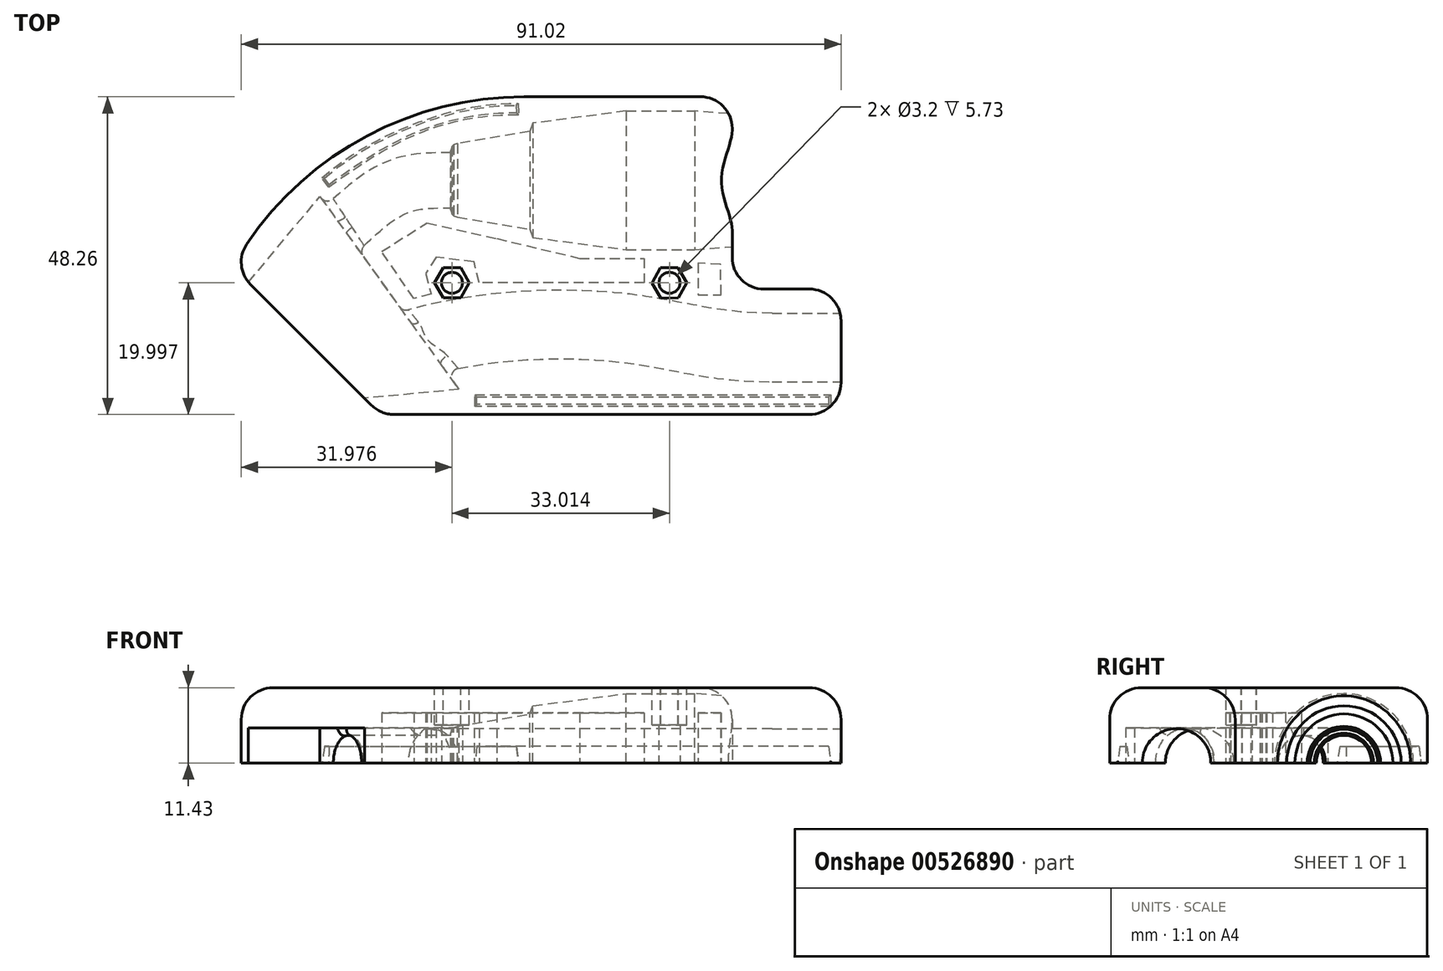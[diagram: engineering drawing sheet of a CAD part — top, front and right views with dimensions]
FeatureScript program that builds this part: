
annotation { "Feature Type Name" : "Feature", "Feature Type Description" : "" }
export const myFeature = defineFeature(function(context is Context, id is Id, definition is map)
    precondition{}
    {
        {
            var Q0;
            Q0=qCreatedBy(makeId("Top.planeOp"),FACE);
            var sketch = newSketch(context, id + "F0", { "sketchPlane" : qUnion([Q0])});
            skLineSegment(sketch, "E0", {"start": v(-28.61, 2.44) * mm, "end": v(45.8, 2.44) * mm});
            skLineSegment(sketch, "E1", {"start": v(45.8, 2.44) * mm, "end": v(45.8, -5.69) * mm});
            skLineSegment(sketch, "E2", {"start": v(45.8, -5.69) * mm, "end": v(33.96, -5.69) * mm});
            skLineSegment(sketch, "E3", {"start": v(33.96, -5.69) * mm, "end": v(31.07, -7.5) * mm});
            skLineSegment(sketch, "E4", {"start": v(31.07, -7.5) * mm, "end": v(15.98, -7.5) * mm});
            skLineSegment(sketch, "E5", {"start": v(15.98, -7.5) * mm, "end": v(8.33, -8.1) * mm});
            skLineSegment(sketch, "E6", {"start": v(8.33, -8.1) * mm, "end": v(-2.02, -8.1) * mm});
            skLineSegment(sketch, "E7", {"start": v(-2.02, -8.1) * mm, "end": v(-16.21, -6.24) * mm});
            skLineSegment(sketch, "E8", {"start": v(-16.21, -6.24) * mm, "end": v(-16.67, -5) * mm});
            skLineSegment(sketch, "E9", {"start": v(-16.67, -5) * mm, "end": v(-27.65, -3.12) * mm});
            skLineSegment(sketch, "E10", {"start": v(-27.65, -3.12) * mm, "end": v(-28.19, -2.96) * mm});
            skLineSegment(sketch, "E11", {"start": v(-28.19, -2.96) * mm, "end": v(-28.49, -2.68) * mm});
            skLineSegment(sketch, "E12", {"start": v(-28.49, -2.68) * mm, "end": v(-28.63, -2.06) * mm});
            skLineSegment(sketch, "E13", {"start": v(-28.63, -2.06) * mm, "end": v(-28.61, 2.44) * mm});
            skLineSegment(sketch, "E14.bottom", {"start": v(20.09, -22.96) * mm, "end": v(33.96, -22.96) * mm});
            skLineSegment(sketch, "E14.top", {"start": v(20.09, -28.16) * mm, "end": v(33.96, -28.16) * mm});
            skLineSegment(sketch, "E14.left", {"start": v(20.09, -22.96) * mm, "end": v(20.09, -28.16) * mm});
            skLineSegment(sketch, "E14.right", {"start": v(33.96, -22.96) * mm, "end": v(33.96, -28.16) * mm});
            skLineSegment(sketch, "E15", {"start": v(33.96, -25.56) * mm, "end": v(42.75, -25.56) * mm});
            skLineSegment(sketch, "E16", {"start": v(42.75, -25.56) * mm, "end": v(42.75, -22.97) * mm});
            skLineSegment(sketch, "E17", {"start": v(42.75, -22.97) * mm, "end": v(33.96, -22.96) * mm});
            skLineSegment(sketch, "E18.MirrorCS", {"start": v(45.8, 2.44) * mm, "end": v(45.8, 10.57) * mm});
            skLineSegment(sketch, "E19.MirrorCS", {"start": v(45.8, 10.57) * mm, "end": v(33.96, 10.57) * mm});
            skLineSegment(sketch, "E20.MirrorCS", {"start": v(33.96, 10.57) * mm, "end": v(31.07, 12.39) * mm});
            skLineSegment(sketch, "E21.MirrorCS", {"start": v(31.07, 12.39) * mm, "end": v(15.98, 12.39) * mm});
            skLineSegment(sketch, "E22.MirrorCS", {"start": v(15.98, 12.39) * mm, "end": v(8.33, 12.98) * mm});
            skLineSegment(sketch, "E23.MirrorCS", {"start": v(8.33, 12.98) * mm, "end": v(-2.02, 12.98) * mm});
            skLineSegment(sketch, "E24.MirrorCS", {"start": v(-2.02, 12.98) * mm, "end": v(-16.21, 11.12) * mm});
            skLineSegment(sketch, "E25.MirrorCS", {"start": v(-28.19, 7.85) * mm, "end": v(-28.49, 7.56) * mm});
            skLineSegment(sketch, "E26.MirrorCS", {"start": v(-16.21, 11.12) * mm, "end": v(-16.67, 9.89) * mm});
            skLineSegment(sketch, "E27.MirrorCS", {"start": v(-27.65, 8) * mm, "end": v(-28.19, 7.85) * mm});
            skLineSegment(sketch, "E28.MirrorCS", {"start": v(-28.49, 7.56) * mm, "end": v(-28.63, 6.94) * mm});
            skLineSegment(sketch, "E29.MirrorCS", {"start": v(-28.63, 6.94) * mm, "end": v(-28.61, 2.44) * mm});
            skLineSegment(sketch, "E30.MirrorCS", {"start": v(-16.67, 9.89) * mm, "end": v(-27.65, 8) * mm});
            skLineSegment(sketch, "E31.MirrorCS", {"start": v(20.09, -17.75) * mm, "end": v(33.96, -17.75) * mm});
            skLineSegment(sketch, "E32.MirrorCS", {"start": v(20.09, -22.96) * mm, "end": v(20.09, -17.75) * mm});
            skLineSegment(sketch, "E33.MirrorCS", {"start": v(33.96, -22.96) * mm, "end": v(33.96, -17.75) * mm});
            skLineSegment(sketch, "E34.MirrorCS", {"start": v(33.96, -20.35) * mm, "end": v(42.75, -20.35) * mm});
            skLineSegment(sketch, "E35.MirrorCS", {"start": v(42.75, -20.35) * mm, "end": v(42.75, -22.95) * mm});
            skSolve(sketch);
        }
        {
            var Q0;
            Q0=qCreatedBy(makeId("Top.planeOp"),FACE);
            var sketch = newSketch(context, id + "F1", { "sketchPlane" : qUnion([Q0])});
            skLineSegment(sketch, "E36", {"start": v(30.56, -33.12) * mm, "end": v(-39.3, -33.12) * mm});
            skLineSegment(sketch, "E37", {"start": v(14.05, 15.14) * mm, "end": v(-17.52, 15.14) * mm});
            skPoint(sketch, "E38.visualSharp", {"position": v(-60.88, 15.14) * mm});
            skArc(sketch, "E38.filletArc", {"start": v(-17.52, 15.14) * mm, "mid": v(-43.12, 8.22) * mm, "end": v(-61.74, -10.67) * mm});
            skLineSegment(sketch, "E39", {"start": v(14.05, 15.14) * mm, "end": v(14.05, -14.07) * mm});
            skLineSegment(sketch, "E40", {"start": v(14.05, -14.07) * mm, "end": v(30.56, -14.07) * mm});
            skLineSegment(sketch, "E41", {"start": v(30.56, -14.07) * mm, "end": v(30.56, -33.12) * mm});
            skLineSegment(sketch, "E42", {"start": v(-39.3, -33.12) * mm, "end": v(-61.74, -10.67) * mm});
            skSolve(sketch);
        }
        {
            var Q0;
            Q0 = qSketchRegion(id + "F1", true);
            extrude(context, id + "F2", {"entities" : qUnion([Q0]), "depth" : 11.43 * mm, "offsetDistance" : 25.4 * mm});
        }
        {
            var Q0;
            Q0=makeQuery(id+"F0.imprint","IMPRINT",FACE,{"disambiguationData":[TD([[makeQuery(id+"F0.imprint","IMPRINT",EDGE,{"derivedFrom":sQuery(id+"F0.wireOp",EDGE,"E0")}),-1.0]])]});
            var Q1;
            Q1=sQuery(id+"F0.wireOp",EDGE,"E0");
            revolve(context, id + "F3", {"operationType" : NewBodyOperationType.REMOVE, "entities" : qUnion([Q0]), "axis" : qUnion([Q1]), "revolveType" : RevolveType.FULL, "oppositeDirection" : true});
        }
        {
            var Q0;
            {var subQ1=sQuery(id+"F0.wireOp",EDGE,"E14.bottom");Q0=makeQuery(id+"F0.imprint","IMPRINT",FACE,{"disambiguationData":[TD([[makeQuery(id+"F0.imprint","IMPRINT",EDGE,{"derivedFrom":subQ1}),-1.0]])]});}
            var Q1;
            Q1=sQuery(id+"F0.wireOp",EDGE,"E14.bottom");
            revolve(context, id + "F4", {"operationType" : NewBodyOperationType.REMOVE, "entities" : qUnion([Q0]), "axis" : qUnion([Q1]), "revolveType" : RevolveType.FULL, "oppositeDirection" : true});
        }
        {
            var Q0;
            Q0=makeQuery(id+"F0.imprint","IMPRINT",FACE,{"disambiguationData":[TD([[makeQuery(id+"F0.imprint","IMPRINT",EDGE,{"derivedFrom":sQuery(id+"F0.wireOp",EDGE,"E0")}),-1.0]])]});
            var sketch = newSketch(context, id + "F5", { "sketchPlane" : qUnion([Q0])});
            skLineSegment(sketch, "E43.0", {"start": v(-28.61, 2.44) * mm, "end": v(45.8, 2.44) * mm});
            skFitSpline(sketch, "E44", {"points": [v(-28.61, 2.44) * mm, v(-39.42, 0) * mm, v(-59.5, -21) * mm], "startDerivative": vector(-33.23, 0.1) * mm, "endDerivative": vector(-30.01, -33.42) * mm});
            skSolve(sketch);
        }
        {
            var Q0;
            Q0=sQuery(id+"F5.wireOp",VERTEX,"E43.0.start");
            var Q1;
            Q1=sQuery(id+"F5.wireOp",EDGE,"E43.0");
            cPlane(context, id + "F6", {"entities" : qUnion([Q0, Q1]), "cplaneType" : CPlaneType.LINE_POINT, "offset" : 25.4 * mm, "width" : 152.4 * mm, "height" : 152.4 * mm});
        }
        {
            var Q0;
            Q0=qCreatedBy(id+"F6.planeOp",FACE);
            var sketch = newSketch(context, id + "F7", { "sketchPlane" : qUnion([Q0])});
            skCircle(sketch, "E45", {"center": v(2.44, 0) * mm, "radius": 4.2 * mm});
            skSolve(sketch);
        }
        {
            var Q0;
            Q0 = qSketchRegion(id + "F7", true);
            var Q1;
            Q1=sQuery(id+"F5.wireOp",EDGE,"E44");
            sweep(context, id + "F8", {"operationType" : NewBodyOperationType.REMOVE, "profiles" : qUnion([Q0]), "path" : qUnion([Q1])});
        }
        {
            var Q0;
            Q0=makeQuery(id+"F1.imprint","IMPRINT",FACE,{"disambiguationData":[TD([[makeQuery(id+"F1.imprint","IMPRINT",EDGE,{"derivedFrom":sQuery(id+"F1.wireOp",EDGE,"E36")}),-1.0]])]});
            var sketch = newSketch(context, id + "F9", { "sketchPlane" : qUnion([Q0])});
            skLineSegment(sketch, "E46.0", {"start": v(20.09, -22.96) * mm, "end": v(33.96, -22.96) * mm});
            skFitSpline(sketch, "E47", {"points": [v(20.09, -22.96) * mm, v(0, -20.3) * mm, v(-30.17, -21.36) * mm, v(-60.66, -38.27) * mm], "startDerivative": vector(-92.11, 0.42) * mm, "endDerivative": vector(-55.97, -70.64) * mm});
            skSolve(sketch);
        }
        {
            var Q0;
            Q0=sQuery(id+"F9.wireOp",VERTEX,"E46.0.start");
            var Q1;
            Q1=sQuery(id+"F0.wireOp",EDGE,"E14.bottom");
            cPlane(context, id + "F10", {"entities" : qUnion([Q0, Q1]), "cplaneType" : CPlaneType.LINE_POINT, "offset" : 25.4 * mm, "width" : 152.4 * mm, "height" : 152.4 * mm});
        }
        {
            var Q0;
            Q0=qCreatedBy(id+"F10.planeOp",FACE);
            var sketch = newSketch(context, id + "F11", { "sketchPlane" : qUnion([Q0])});
            skCircle(sketch, "E48", {"center": v(-22.96, 0) * mm, "radius": 5.2 * mm});
            skSolve(sketch);
        }
        {
            var Q0;
            Q0 = qSketchRegion(id + "F11", true);
            var Q1;
            Q1=sQuery(id+"F9.wireOp",EDGE,"E47");
            sweep(context, id + "F12", {"operationType" : NewBodyOperationType.REMOVE, "profiles" : qUnion([Q0]), "path" : qUnion([Q1])});
        }
        {
            var Q0;
            Q0=makeQuery(id+"F1.imprint","IMPRINT",FACE,{"disambiguationData":[TD([[makeQuery(id+"F1.imprint","IMPRINT",EDGE,{"derivedFrom":sQuery(id+"F1.wireOp",EDGE,"E36")}),-1.0]])]});
            var sketch = newSketch(context, id + "F13", { "sketchPlane" : qUnion([Q0])});
            skLineSegment(sketch, "E49.0", {"start": v(-39.3, -33.12) * mm, "end": v(-61.74, -10.67) * mm});
            skLineSegment(sketch, "E50", {"start": v(-59.38, -13.03) * mm, "end": v(-48.5, 0) * mm});
            skLineSegment(sketch, "E51", {"start": v(-48.5, 0) * mm, "end": v(-27.45, -29.3) * mm});
            skLineSegment(sketch, "E52", {"start": v(-27.45, -29.3) * mm, "end": v(-41.75, -30.66) * mm});
            skSolve(sketch);
        }
        {
            var Q0;
            Q0 = qSketchRegion(id + "F13", true);
            extrude(context, id + "F14", {"entities" : qUnion([Q0]), "operationType" : NewBodyOperationType.REMOVE, "depth" : 5.33 * mm, "offsetDistance" : 25.4 * mm});
        }
        {
            var Q0;
            Q0=makeQuery(id+"F1.imprint","IMPRINT",FACE,{"disambiguationData":[TD([[makeQuery(id+"F1.imprint","IMPRINT",EDGE,{"derivedFrom":sQuery(id+"F1.wireOp",EDGE,"E36")}),-1.0]])]});
            var sketch = newSketch(context, id + "F15", { "sketchPlane" : qUnion([Q0])});
            skCircle(sketch, "E53", {"center": v(-28.48, -13.12) * mm, "radius": 1.6 * mm});
            skCircle(sketch, "E54", {"center": v(4.53, -13.12) * mm, "radius": 1.6 * mm});
            skSolve(sketch);
        }
        {
            var Q0;
            Q0 = qSketchRegion(id + "F15", true);
            extrude(context, id + "F16", {"entities" : qUnion([Q0]), "operationType" : NewBodyOperationType.REMOVE, "oppositeDirection" : true, "depth" : 25.4 * mm, "offsetDistance" : 25.4 * mm});
        }
        {
            var Q0;
            Q0=qCreatedBy(makeId("Top.planeOp"),FACE);
            var sketch = newSketch(context, id + "F17", { "sketchPlane" : qUnion([Q0])});
            skFitSpline(sketch, "E55", {"points": [v(-48.22, 2.83) * mm, v(-33.89, 11.13) * mm, v(-18.43, 14.15) * mm], "startDerivative": vector(25.54, 22.54) * mm, "endDerivative": vector(34.87, -0.06) * mm});
            skLineSegment(sketch, "E56", {"start": v(-48.22, 2.83) * mm, "end": v(-47.2, 1.4) * mm});
            skFitSpline(sketch, "E57", {"points": [v(-47.2, 1.4) * mm, v(-33.83, 9.46) * mm, v(-18.38, 12.4) * mm], "startDerivative": vector(25.56, 18.7) * mm, "endDerivative": vector(32.76, -0.78) * mm});
            skLineSegment(sketch, "E58", {"start": v(-18.38, 12.4) * mm, "end": v(-18.43, 14.15) * mm});
            skLineSegment(sketch, "E59", {"start": v(-25, -31.9) * mm, "end": v(29.01, -31.9) * mm});
            skLineSegment(sketch, "E60", {"start": v(29.01, -31.9) * mm, "end": v(29.01, -30.14) * mm});
            skLineSegment(sketch, "E61", {"start": v(29.01, -30.14) * mm, "end": v(-25, -30.14) * mm});
            skLineSegment(sketch, "E62", {"start": v(-25, -30.14) * mm, "end": v(-25, -31.9) * mm});
            skSolve(sketch);
        }
        {
            var Q0;
            Q0=makeQuery(id+"F2.opExtrude","SWEPT_EDGE",EDGE,{"disambiguationData":[OSD([sQuery(id+"F1.wireOp",EDGE,"E38.filletArc"),sQuery(id+"F1.wireOp",EDGE,"E42")])]});
            var Q1;
            Q1=makeQuery(id+"F2.opExtrude","CAP_EDGE",EDGE,{"disambiguationData":[OSD([sQuery(id+"F1.wireOp",EDGE,"E38.filletArc")])],"isStart":false});
            var Q2;
            Q2=makeQuery(id+"F2.opExtrude","CAP_EDGE",EDGE,{"disambiguationData":[OSD([sQuery(id+"F1.wireOp",EDGE,"E42")])],"isStart":false});
            var Q3;
            Q3=makeQuery(id+"F2.opExtrude","CAP_EDGE",EDGE,{"disambiguationData":[OSD([sQuery(id+"F1.wireOp",EDGE,"E36")])],"isStart":false});
            var Q4;
            Q4=makeQuery(id+"F2.opExtrude","SWEPT_EDGE",EDGE,{"disambiguationData":[OSD([sQuery(id+"F1.wireOp",EDGE,"E36"),sQuery(id+"F1.wireOp",EDGE,"E42")])]});
            var Q5;
            Q5=makeQuery(id+"F2.opExtrude","SWEPT_EDGE",EDGE,{"disambiguationData":[OSD([sQuery(id+"F1.wireOp",EDGE,"E36"),sQuery(id+"F1.wireOp",EDGE,"E41")])]});
            var Q6;
            Q6=makeQuery(id+"F2.opExtrude","SWEPT_EDGE",EDGE,{"disambiguationData":[OSD([sQuery(id+"F1.wireOp",EDGE,"E40"),sQuery(id+"F1.wireOp",EDGE,"E41")])]});
            var Q7;
            Q7=makeQuery(id+"F2.opExtrude","SWEPT_EDGE",EDGE,{"disambiguationData":[OSD([sQuery(id+"F1.wireOp",EDGE,"E39"),sQuery(id+"F1.wireOp",EDGE,"E40")])]});
            var Q8;
            Q8=makeQuery(id+"F2.opExtrude","CAP_EDGE",EDGE,{"disambiguationData":[OSD([sQuery(id+"F1.wireOp",EDGE,"E41")])],"isStart":false});
            var Q9;
            Q9=makeQuery(id+"F2.opExtrude","CAP_EDGE",EDGE,{"disambiguationData":[OSD([sQuery(id+"F1.wireOp",EDGE,"E40")])],"isStart":false});
            var Q10;
            Q10=makeQuery(id+"F2.opExtrude","CAP_EDGE",EDGE,{"disambiguationData":[OSD([sQuery(id+"F1.wireOp",EDGE,"E39")])],"isStart":false});
            var Q11;
            Q11=makeQuery(id+"F2.opExtrude","CAP_EDGE",EDGE,{"disambiguationData":[OSD([sQuery(id+"F1.wireOp",EDGE,"E37")])],"isStart":false});
            var Q12;
            Q12=makeQuery(id+"F2.opExtrude","SWEPT_EDGE",EDGE,{"disambiguationData":[OSD([sQuery(id+"F1.wireOp",EDGE,"E37"),sQuery(id+"F1.wireOp",EDGE,"E39")])]});
            fillet(context, id + "F18", {"entities" : qUnion([Q0, Q1, Q2, Q3, Q4, Q5, Q6, Q7, Q8, Q9, Q10, Q11, Q12]), "radius" : 4.83 * mm, "tangentPropagation" : true, "allowEdgeOverflow" : false});
        }
        {
            var Q0;
            Q0=qCreatedBy(makeId("Top.planeOp"),FACE);
            var sketch = newSketch(context, id + "F19", { "sketchPlane" : qUnion([Q0])});
            skLineSegment(sketch, "E63", {"start": v(-39.15, -8.36) * mm, "end": v(-32.26, -4.02) * mm});
            skLineSegment(sketch, "E64", {"start": v(-32.26, -4.02) * mm, "end": v(-21.67, -6.4) * mm});
            skLineSegment(sketch, "E65", {"start": v(-21.67, -6.4) * mm, "end": v(-9.1, -9.4) * mm});
            skLineSegment(sketch, "E66", {"start": v(-9.1, -9.4) * mm, "end": v(0.69, -9.4) * mm});
            skLineSegment(sketch, "E67", {"start": v(0.69, -9.4) * mm, "end": v(0.69, -13.1) * mm});
            skLineSegment(sketch, "E68", {"start": v(0.69, -13.1) * mm, "end": v(-21.6, -13.1) * mm});
            skLineSegment(sketch, "E69", {"start": v(-21.6, -13.1) * mm, "end": v(-24.34, -13.1) * mm});
            skLineSegment(sketch, "E70", {"start": v(-24.34, -13.1) * mm, "end": v(-25.11, -9.94) * mm});
            skLineSegment(sketch, "E71", {"start": v(-25.11, -9.94) * mm, "end": v(-30.9, -9.24) * mm});
            skLineSegment(sketch, "E72", {"start": v(-30.9, -9.24) * mm, "end": v(-32.48, -11.7) * mm});
            skLineSegment(sketch, "E73", {"start": v(-32.48, -11.7) * mm, "end": v(-31.64, -14.8) * mm});
            skLineSegment(sketch, "E74", {"start": v(-31.64, -14.8) * mm, "end": v(-34.27, -15.52) * mm});
            skLineSegment(sketch, "E75", {"start": v(-34.27, -15.52) * mm, "end": v(-39.15, -8.36) * mm});
            skLineSegment(sketch, "E76", {"start": v(8.84, -10.13) * mm, "end": v(8.84, -14.95) * mm});
            skLineSegment(sketch, "E77", {"start": v(8.84, -14.95) * mm, "end": v(12.38, -14.95) * mm});
            skLineSegment(sketch, "E78", {"start": v(12.38, -14.95) * mm, "end": v(12.27, -10.3) * mm});
            skLineSegment(sketch, "E79", {"start": v(12.27, -10.3) * mm, "end": v(8.84, -10.13) * mm});
            skSolve(sketch);
        }
        {
            var Q0;
            Q0 = qSketchRegion(id + "F19", true);
            extrude(context, id + "F20", {"entities" : qUnion([Q0]), "operationType" : NewBodyOperationType.REMOVE, "depth" : 7.62 * mm, "offsetDistance" : 25.4 * mm});
        }
        {
            var Q0;
            Q0 = qSketchRegion(id + "F15", true);
            extrude(context, id + "F21", {"entities" : qUnion([Q0]), "operationType" : NewBodyOperationType.REMOVE, "depth" : 25.4 * mm, "offsetDistance" : 25.4 * mm});
        }
        {
            var Q0;
            Q0=makeQuery(id+"F2.opExtrude","CAP_FACE",FACE,{"disambiguationData":[OSD([sQuery(id+"F1.wireOp",EDGE,"E36"),sQuery(id+"F1.wireOp",EDGE,"E37"),sQuery(id+"F1.wireOp",EDGE,"E38.filletArc"),sQuery(id+"F1.wireOp",EDGE,"E39"),sQuery(id+"F1.wireOp",EDGE,"E40"),sQuery(id+"F1.wireOp",EDGE,"E41"),sQuery(id+"F1.wireOp",EDGE,"E42")])],"isStart":false});
            var sketch = newSketch(context, id + "F22", { "sketchPlane" : qUnion([Q0])});
            skCircle(sketch, "E80.0", {"center": v(-28.48, -13.12) * mm, "radius": 1.6 * mm});
            skCircle(sketch, "E81.0", {"center": v(4.53, -13.12) * mm, "radius": 1.6 * mm});
            skCircle(sketch, "E82.cCircle", {"center": v(-28.48, -13.12) * mm, "radius": 2.65 * mm, "construction": true});
            skLineSegment(sketch, "E82.0", {"start": v(-27.16, -15.42) * mm, "end": v(-29.81, -15.41) * mm});
            skLineSegment(sketch, "E82.1", {"start": v(-29.81, -15.41) * mm, "end": v(-31.13, -13.12) * mm});
            skLineSegment(sketch, "E82.2", {"start": v(-31.13, -13.12) * mm, "end": v(-29.8, -10.82) * mm});
            skLineSegment(sketch, "E82.3", {"start": v(-29.8, -10.82) * mm, "end": v(-27.15, -10.83) * mm});
            skLineSegment(sketch, "E82.4", {"start": v(-27.15, -10.83) * mm, "end": v(-25.83, -13.13) * mm});
            skLineSegment(sketch, "E82.5", {"start": v(-25.83, -13.13) * mm, "end": v(-27.16, -15.42) * mm});
            skCircle(sketch, "E83.cCircle", {"center": v(4.53, -13.12) * mm, "radius": 2.65 * mm, "construction": true});
            skLineSegment(sketch, "E83.0", {"start": v(5.88, -15.4) * mm, "end": v(3.23, -15.43) * mm});
            skLineSegment(sketch, "E83.1", {"start": v(3.23, -15.43) * mm, "end": v(1.88, -13.15) * mm});
            skLineSegment(sketch, "E83.2", {"start": v(1.88, -13.15) * mm, "end": v(3.18, -10.84) * mm});
            skLineSegment(sketch, "E83.3", {"start": v(3.18, -10.84) * mm, "end": v(5.83, -10.82) * mm});
            skLineSegment(sketch, "E83.4", {"start": v(5.83, -10.82) * mm, "end": v(7.18, -13.1) * mm});
            skLineSegment(sketch, "E83.5", {"start": v(7.18, -13.1) * mm, "end": v(5.88, -15.4) * mm});
            skSolve(sketch);
        }
        {
            var Q0;
            Q0 = qSketchRegion(id + "F22", true);
            extrude(context, id + "F23", {"entities" : qUnion([Q0]), "operationType" : NewBodyOperationType.REMOVE, "oppositeDirection" : true, "depth" : 5.7 * mm, "offsetDistance" : 25.4 * mm});
        }
        {
            var Q0;
            Q0=makeQuery(id+"F14.boolean.opBoolean","INTERSECT",EDGE,{"derivedFrom":[makeQuery(id+"F12.boolean.opBoolean","COPY",FACE,{"derivedFrom":makeQuery(id+"F12.opSweep","SWEPT_FACE",FACE,{"disambiguationData":[OSD([sQuery(id+"F9.wireOp",EDGE,"E47"),sQuery(id+"F11.wireOp",EDGE,"E48")])]})}),makeQuery(id+"F14.opExtrude","SWEPT_FACE",FACE,{"disambiguationData":[OSD([sQuery(id+"F13.wireOp",EDGE,"E51")])]})]});
            var Q1;
            Q1=makeQuery(id+"F14.boolean.opBoolean","INTERSECT",EDGE,{"derivedFrom":[makeQuery(id+"F8.boolean.opBoolean","COPY",FACE,{"derivedFrom":makeQuery(id+"F8.opSweep","SWEPT_FACE",FACE,{"disambiguationData":[OSD([sQuery(id+"F5.wireOp",EDGE,"E44"),sQuery(id+"F7.wireOp",EDGE,"E45")])]})}),makeQuery(id+"F14.opExtrude","SWEPT_FACE",FACE,{"disambiguationData":[OSD([sQuery(id+"F13.wireOp",EDGE,"E51")])]})]});
            var Q2;
            Q2=makeQuery(id+"F14.boolean.opBoolean","COPY",EDGE,{"derivedFrom":makeQuery(id+"F14.opExtrude","SWEPT_EDGE",EDGE,{"disambiguationData":[OSD([sQuery(id+"F13.wireOp",EDGE,"E49.0"),sQuery(id+"F13.wireOp",EDGE,"E50")])]})});
            var Q3;
            Q3=makeQuery(id+"F14.boolean.opBoolean","COPY",EDGE,{"derivedFrom":makeQuery(id+"F14.opExtrude","SWEPT_EDGE",EDGE,{"disambiguationData":[OSD([sQuery(id+"F13.wireOp",EDGE,"E49.0"),sQuery(id+"F13.wireOp",EDGE,"E52")])]})});
            fillet(context, id + "F24", {"entities" : qUnion([Q0, Q1, Q2, Q3]), "radius" : 1.27 * mm, "tangentPropagation" : true, "allowEdgeOverflow" : false});
        }
        {
            var Q0;
            Q0 = qSketchRegion(id + "F17", true);
            extrude(context, id + "F25", {"entities" : qUnion([Q0]), "operationType" : NewBodyOperationType.REMOVE, "depth" : 2.5 * mm, "offsetDistance" : 25.4 * mm, "hasDraft" : true, "draftAngle" : 7 * degree, "draftPullDirection" : true});
        }
    });
